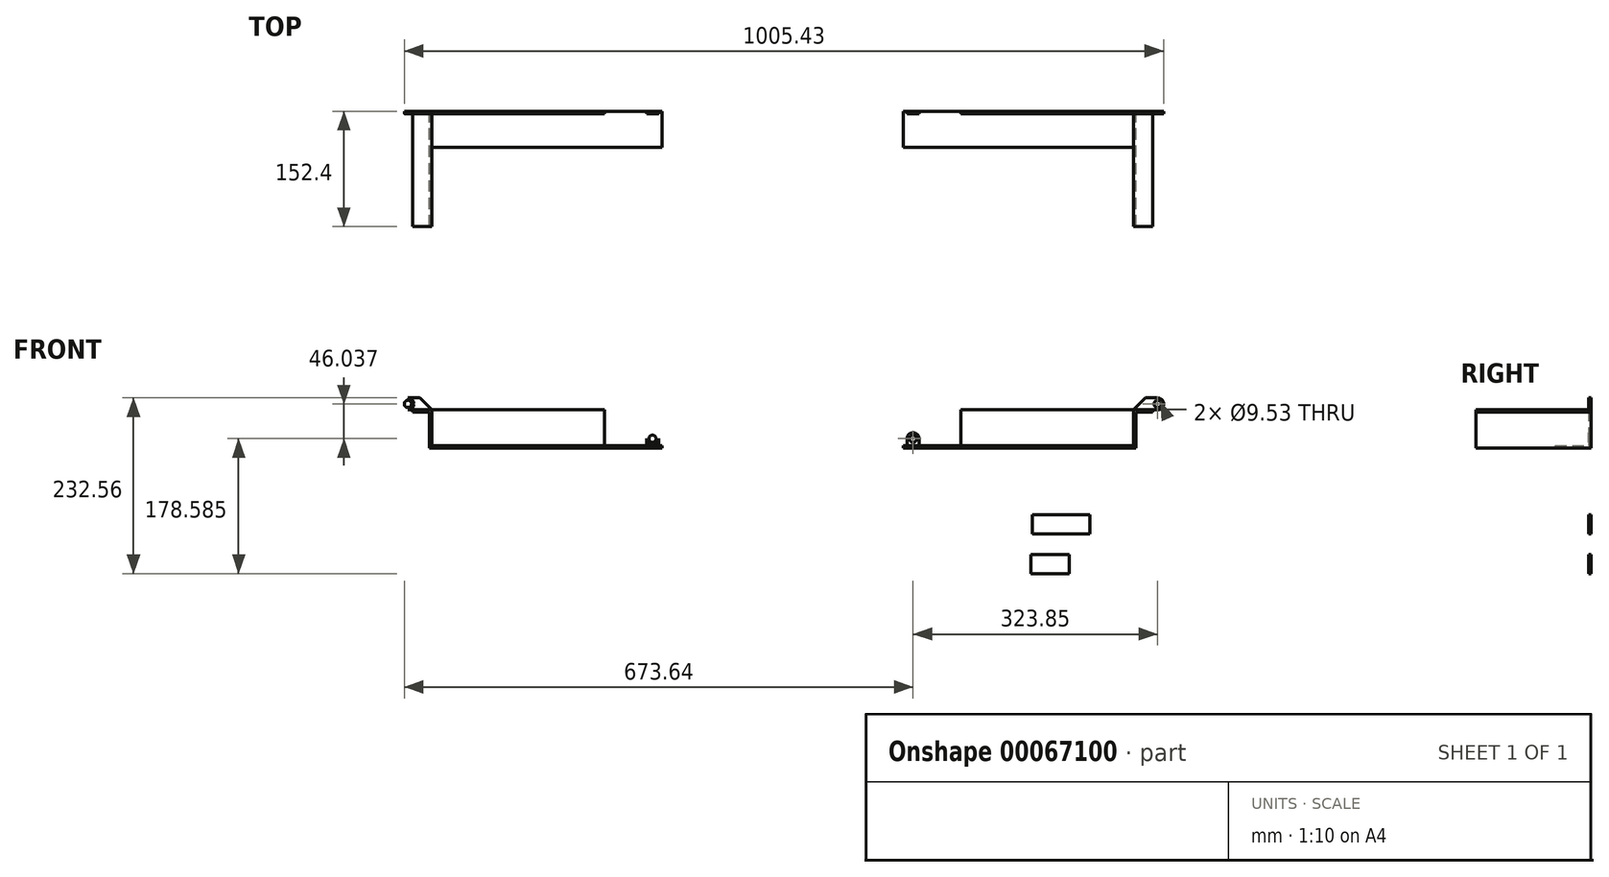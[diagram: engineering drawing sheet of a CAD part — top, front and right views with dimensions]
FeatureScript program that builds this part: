
annotation { "Feature Type Name" : "Feature", "Feature Type Description" : "" }
export const myFeature = defineFeature(function(context is Context, id is Id, definition is map)
    precondition{}
    {
        {
            var Q0;
            Q0=qCreatedBy(makeId("Front.planeOp"),FACE);
            var sketch = newSketch(context, id + "F0", { "sketchPlane" : qUnion([Q0])});
            skLineSegment(sketch, "E0", {"start": v(120.09, 92.83) * mm, "end": v(94.69, 92.83) * mm});
            skLineSegment(sketch, "E1", {"start": v(94.69, 92.83) * mm, "end": v(94.69, 42.03) * mm});
            skLineSegment(sketch, "E2", {"start": v(94.69, 42.03) * mm, "end": v(97.86, 42.03) * mm});
            skLineSegment(sketch, "E3", {"start": v(97.86, 42.03) * mm, "end": v(97.86, 89.66) * mm});
            skLineSegment(sketch, "E4", {"start": v(97.86, 89.66) * mm, "end": v(120.09, 89.66) * mm});
            skLineSegment(sketch, "E5", {"start": v(120.09, 89.66) * mm, "end": v(120.09, 92.83) * mm});
            skLineSegment(sketch, "E6", {"start": v(94.69, 92.83) * mm, "end": v(-133.91, 92.83) * mm});
            skLineSegment(sketch, "E7", {"start": v(-133.91, 92.83) * mm, "end": v(-133.91, 42.03) * mm});
            skLineSegment(sketch, "E8", {"start": v(-133.91, 42.03) * mm, "end": v(94.69, 42.03) * mm});
            skLineSegment(sketch, "E9", {"start": v(-133.91, 42.03) * mm, "end": v(-210.11, 42.03) * mm});
            skLineSegment(sketch, "E10", {"start": v(-210.11, 42.03) * mm, "end": v(-210.11, 45.2) * mm});
            skLineSegment(sketch, "E11", {"start": v(-210.11, 45.2) * mm, "end": v(-133.91, 45.2) * mm});
            skLineSegment(sketch, "E12", {"start": v(-184.71, 45.2) * mm, "end": v(-184.71, 42.03) * mm});
            skLineSegment(sketch, "E13", {"start": v(-184.71, 42.03) * mm, "end": v(-159.31, 42.03) * mm});
            skLineSegment(sketch, "E14", {"start": v(-159.31, 42.03) * mm, "end": v(-159.31, 45.2) * mm});
            skCircle(sketch, "E15", {"center": v(-197.41, 54.73) * mm, "radius": 7.94 * mm});
            skLineSegment(sketch, "E16", {"start": v(-205.35, 54.73) * mm, "end": v(-205.35, 45.2) * mm});
            skLineSegment(sketch, "E17", {"start": v(-189.47, 54.73) * mm, "end": v(-189.47, 45.2) * mm});
            skCircle(sketch, "E18", {"center": v(-197.41, 54.73) * mm, "radius": 4.76 * mm});
            skCircle(sketch, "E19", {"center": v(126.44, 100.77) * mm, "radius": 7.94 * mm});
            skCircle(sketch, "E20", {"center": v(126.44, 100.77) * mm, "radius": 4.76 * mm});
            skLineSegment(sketch, "E21", {"start": v(120.09, 92.83) * mm, "end": v(126.44, 92.83) * mm});
            skLineSegment(sketch, "E22", {"start": v(94.69, 92.83) * mm, "end": v(110.56, 108.7) * mm});
            skLineSegment(sketch, "E23", {"start": v(110.56, 108.7) * mm, "end": v(126.44, 108.7) * mm});
            skLineSegment(sketch, "E24", {"start": v(-184.71, 42.03) * mm, "end": v(-159.31, 45.2) * mm, "construction": true});
            skLineSegment(sketch, "E25", {"start": v(-197.41, 40.48) * mm, "end": v(-197.41, 98.92) * mm, "construction": true});
            skLineSegment(sketch, "E26", {"start": v(-210.11, 42.03) * mm, "end": v(-184.71, 45.2) * mm, "construction": true});
            skLineSegment(sketch, "E27", {"start": v(-197.41, 43.62) * mm, "end": v(-197.41, 100.75) * mm, "construction": true});
            skLineSegment(sketch, "E28", {"start": v(-369.92, 208.5) * mm, "end": v(-369.92, -62.68) * mm, "construction": true});
            skLineSegment(sketch, "E29.MirrorCS", {"start": v(-529.74, 42.03) * mm, "end": v(-555.14, 45.2) * mm, "construction": true});
            skLineSegment(sketch, "E30.MirrorCS", {"start": v(-550.38, 54.73) * mm, "end": v(-550.38, 45.2) * mm});
            skLineSegment(sketch, "E31.MirrorCS", {"start": v(-834.54, 42.03) * mm, "end": v(-837.71, 42.03) * mm});
            skLineSegment(sketch, "E32.MirrorCS", {"start": v(-529.74, 42.03) * mm, "end": v(-529.74, 45.2) * mm});
            skLineSegment(sketch, "E33.MirrorCS", {"start": v(-534.5, 54.73) * mm, "end": v(-534.5, 45.2) * mm});
            skLineSegment(sketch, "E34.MirrorCS", {"start": v(-859.94, 92.83) * mm, "end": v(-866.29, 92.83) * mm});
            skCircle(sketch, "E35.MirrorC", {"center": v(-866.29, 100.77) * mm, "radius": 4.76 * mm});
            skLineSegment(sketch, "E36.MirrorCS", {"start": v(-555.14, 45.2) * mm, "end": v(-555.14, 42.03) * mm});
            skLineSegment(sketch, "E37.MirrorCS", {"start": v(-859.94, 89.66) * mm, "end": v(-859.94, 92.83) * mm});
            skLineSegment(sketch, "E38.MirrorCS", {"start": v(-555.14, 42.03) * mm, "end": v(-580.54, 45.2) * mm, "construction": true});
            skCircle(sketch, "E39.MirrorC", {"center": v(-542.44, 54.73) * mm, "radius": 4.76 * mm});
            skLineSegment(sketch, "E40.MirrorCS", {"start": v(-580.54, 42.03) * mm, "end": v(-580.54, 45.2) * mm});
            skLineSegment(sketch, "E41.MirrorCS", {"start": v(-555.14, 42.03) * mm, "end": v(-580.54, 42.03) * mm});
            skLineSegment(sketch, "E42.MirrorCS", {"start": v(-542.44, 43.62) * mm, "end": v(-542.44, 100.75) * mm, "construction": true});
            skCircle(sketch, "E43.MirrorC", {"center": v(-866.29, 100.77) * mm, "radius": 7.94 * mm});
            skLineSegment(sketch, "E44.MirrorCS", {"start": v(-850.41, 108.7) * mm, "end": v(-866.29, 108.7) * mm});
            skLineSegment(sketch, "E45.MirrorCS", {"start": v(-542.44, 40.48) * mm, "end": v(-542.44, 98.92) * mm, "construction": true});
            skCircle(sketch, "E46.MirrorC", {"center": v(-542.44, 54.73) * mm, "radius": 7.94 * mm});
            skLineSegment(sketch, "E47.MirrorCS", {"start": v(-529.74, 45.2) * mm, "end": v(-605.94, 45.2) * mm});
            skLineSegment(sketch, "E48.MirrorCS", {"start": v(-605.94, 42.03) * mm, "end": v(-529.74, 42.03) * mm});
            skLineSegment(sketch, "E49.MirrorCS", {"start": v(-834.54, 92.83) * mm, "end": v(-850.41, 108.7) * mm});
            skLineSegment(sketch, "E50.MirrorCS", {"start": v(-859.94, 92.83) * mm, "end": v(-834.54, 92.83) * mm});
            skLineSegment(sketch, "E51.MirrorCS", {"start": v(-837.71, 42.03) * mm, "end": v(-837.71, 89.66) * mm});
            skLineSegment(sketch, "E52.MirrorCS", {"start": v(-837.71, 89.66) * mm, "end": v(-859.94, 89.66) * mm});
            skLineSegment(sketch, "E53.MirrorCS", {"start": v(-834.54, 92.83) * mm, "end": v(-605.94, 92.83) * mm});
            skLineSegment(sketch, "E54.MirrorCS", {"start": v(-605.94, 92.83) * mm, "end": v(-605.94, 42.03) * mm});
            skLineSegment(sketch, "E55.MirrorCS", {"start": v(-834.54, 92.83) * mm, "end": v(-834.54, 42.03) * mm});
            skLineSegment(sketch, "E56.MirrorCS", {"start": v(-605.94, 42.03) * mm, "end": v(-834.54, 42.03) * mm});
            skLineSegment(sketch, "E57", {"start": v(-605.94, 45.2) * mm, "end": v(-834.54, 45.2) * mm});
            skLineSegment(sketch, "E58", {"start": v(-133.91, 45.2) * mm, "end": v(94.69, 45.2) * mm});
            skSolve(sketch);
        }
        {
            var Q0;
            Q0=makeQuery(id+"F0.imprint","IMPRINT",FACE,{"disambiguationData":[TD([[makeQuery(id+"F0.imprint","IMPRINT",EDGE,{"derivedFrom":sQuery(id+"F0.wireOp",EDGE,"E31.MirrorCS")}),-1.0]])]});
            var Q1;
            {var subQ0=sQuery(id+"F0.wireOp",EDGE,"E1");Q1=makeQuery(id+"F0.imprint","IMPRINT",FACE,{"disambiguationData":[TD([[makeQuery(id+"F0.imprint","IMPRINT",EDGE,{"derivedFrom":subQ0}),1.0]])]});}
            extrude(context, id + "F1", {"entities" : qUnion([Q0, Q1]), "depth" : 152.4 * mm});
        }
        {
            var Q0;
            Q0=makeQuery(id+"F0.imprint","IMPRINT",FACE,{"disambiguationData":[TD([[makeQuery(id+"F0.imprint","IMPRINT",EDGE,{"derivedFrom":sQuery(id+"F0.wireOp",EDGE,"E35.MirrorC")}),1.0]])]});
            var Q1;
            {var subQ3=sQuery(id+"F0.wireOp",EDGE,"E34.MirrorCS");Q1=makeQuery(id+"F0.imprint","IMPRINT",FACE,{"disambiguationData":[TD([[makeQuery(id+"F0.imprint","IMPRINT",EDGE,{"derivedFrom":subQ3}),-1.0]])]});}
            var Q2;
            {var subQ1=sQuery(id+"F0.wireOp",EDGE,"E21");Q2=makeQuery(id+"F0.imprint","IMPRINT",FACE,{"disambiguationData":[TD([[makeQuery(id+"F0.imprint","IMPRINT",EDGE,{"derivedFrom":subQ1}),1.0]])]});}
            var Q3;
            Q3=makeQuery(id+"F0.imprint","IMPRINT",FACE,{"disambiguationData":[TD([[makeQuery(id+"F0.imprint","IMPRINT",EDGE,{"derivedFrom":sQuery(id+"F0.wireOp",EDGE,"E20")}),-1.0]])]});
            var Q4;
            {var subQ0=sQuery(id+"F0.wireOp",EDGE,"E30.MirrorCS");Q4=makeQuery(id+"F0.imprint","IMPRINT",FACE,{"disambiguationData":[TD([[makeQuery(id+"F0.imprint","IMPRINT",EDGE,{"derivedFrom":subQ0}),1.0]])]});}
            var Q5;
            Q5=makeQuery(id+"F0.imprint","IMPRINT",FACE,{"disambiguationData":[TD([[makeQuery(id+"F0.imprint","IMPRINT",EDGE,{"derivedFrom":sQuery(id+"F0.wireOp",EDGE,"E39.MirrorC")}),1.0]])]});
            var Q6;
            Q6=makeQuery(id+"F0.imprint","IMPRINT",FACE,{"disambiguationData":[TD([[makeQuery(id+"F0.imprint","IMPRINT",EDGE,{"derivedFrom":sQuery(id+"F0.wireOp",EDGE,"E18")}),-1.0]])]});
            var Q7;
            {var subQ0=sQuery(id+"F0.wireOp",EDGE,"E16");Q7=makeQuery(id+"F0.imprint","IMPRINT",FACE,{"disambiguationData":[TD([[makeQuery(id+"F0.imprint","IMPRINT",EDGE,{"derivedFrom":subQ0}),1.0]])]});}
            extrude(context, id + "F2", {"entities" : qUnion([Q0, Q1, Q2, Q3, Q4, Q5, Q6, Q7]), "depth" : 3.17 * mm});
        }
        {
            var Q0;
            {var subQ2=sQuery(id+"F0.wireOp",EDGE,"E56.MirrorCS");Q0=makeQuery(id+"F0.imprint","IMPRINT",FACE,{"disambiguationData":[TD([[makeQuery(id+"F0.imprint","IMPRINT",EDGE,{"derivedFrom":subQ2}),-1.0]])]});}
            var Q1;
            {var subQ0=sQuery(id+"F0.wireOp",EDGE,"E40.MirrorCS");Q1=makeQuery(id+"F0.imprint","IMPRINT",FACE,{"disambiguationData":[TD([[makeQuery(id+"F0.imprint","IMPRINT",EDGE,{"derivedFrom":subQ0}),1.0]])]});}
            var Q2;
            {var subQ0=sQuery(id+"F0.wireOp",EDGE,"E36.MirrorCS");Q2=makeQuery(id+"F0.imprint","IMPRINT",FACE,{"disambiguationData":[TD([[makeQuery(id+"F0.imprint","IMPRINT",EDGE,{"derivedFrom":subQ0}),-1.0]])]});}
            var Q3;
            {var subQ4=sQuery(id+"F0.wireOp",EDGE,"E32.MirrorCS");Q3=makeQuery(id+"F0.imprint","IMPRINT",FACE,{"disambiguationData":[TD([[makeQuery(id+"F0.imprint","IMPRINT",EDGE,{"derivedFrom":subQ4}),1.0]])]});}
            var Q4;
            {var subQ3=sQuery(id+"F0.wireOp",EDGE,"E10");Q4=makeQuery(id+"F0.imprint","IMPRINT",FACE,{"disambiguationData":[TD([[makeQuery(id+"F0.imprint","IMPRINT",EDGE,{"derivedFrom":subQ3}),-1.0]])]});}
            var Q5;
            {var subQ0=sQuery(id+"F0.wireOp",EDGE,"E12");Q5=makeQuery(id+"F0.imprint","IMPRINT",FACE,{"disambiguationData":[TD([[makeQuery(id+"F0.imprint","IMPRINT",EDGE,{"derivedFrom":subQ0}),1.0]])]});}
            var Q6;
            {var subQ5=sQuery(id+"F0.wireOp",EDGE,"E14");Q6=makeQuery(id+"F0.imprint","IMPRINT",FACE,{"disambiguationData":[TD([[makeQuery(id+"F0.imprint","IMPRINT",EDGE,{"derivedFrom":subQ5}),-1.0]])]});}
            var Q7;
            {var subQ0=sQuery(id+"F0.wireOp",EDGE,"E8");Q7=makeQuery(id+"F0.imprint","IMPRINT",FACE,{"disambiguationData":[TD([[makeQuery(id+"F0.imprint","IMPRINT",EDGE,{"derivedFrom":subQ0}),1.0]])]});}
            extrude(context, id + "F3", {"entities" : qUnion([Q0, Q1, Q2, Q3, Q4, Q5, Q6, Q7]), "depth" : 47.62 * mm});
        }
        {
            var Q0;
            {var subQ0=sQuery(id+"F0.wireOp",EDGE,"E53.MirrorCS");Q0=makeQuery(id+"F0.imprint","IMPRINT",FACE,{"disambiguationData":[TD([[makeQuery(id+"F0.imprint","IMPRINT",EDGE,{"derivedFrom":subQ0}),-1.0]])]});}
            var Q1;
            {var subQ0=sQuery(id+"F0.wireOp",EDGE,"E6");Q1=makeQuery(id+"F0.imprint","IMPRINT",FACE,{"disambiguationData":[TD([[makeQuery(id+"F0.imprint","IMPRINT",EDGE,{"derivedFrom":subQ0}),1.0]])]});}
            extrude(context, id + "F4", {"entities" : qUnion([Q0, Q1]), "depth" : 3.17 * mm});
        }
        {
            var Q0;
            Q0=qCreatedBy(makeId("Front.planeOp"),FACE);
            var sketch = newSketch(context, id + "F5", { "sketchPlane" : qUnion([Q0])});
            skLineSegment(sketch, "E59.bottom", {"start": v(-39.87, -46.07) * mm, "end": v(36.33, -46.07) * mm});
            skLineSegment(sketch, "E59.top", {"start": v(-39.87, -71.47) * mm, "end": v(36.33, -71.47) * mm});
            skLineSegment(sketch, "E59.left", {"start": v(-39.87, -46.07) * mm, "end": v(-39.87, -71.47) * mm});
            skLineSegment(sketch, "E59.right", {"start": v(36.33, -46.07) * mm, "end": v(36.33, -71.47) * mm});
            skLineSegment(sketch, "E60.bottom", {"start": v(-41.78, -98.45) * mm, "end": v(9.02, -98.45) * mm});
            skLineSegment(sketch, "E60.top", {"start": v(-41.78, -123.85) * mm, "end": v(9.02, -123.85) * mm});
            skLineSegment(sketch, "E60.left", {"start": v(-41.78, -98.45) * mm, "end": v(-41.78, -123.85) * mm});
            skLineSegment(sketch, "E60.right", {"start": v(9.02, -98.45) * mm, "end": v(9.02, -123.85) * mm});
            skSolve(sketch);
        }
        {
            var Q0;
            Q0=makeQuery(id+"F5.imprint","IMPRINT",FACE,{"disambiguationData":[TD([[makeQuery(id+"F5.imprint","IMPRINT",EDGE,{"derivedFrom":sQuery(id+"F5.wireOp",EDGE,"E59.bottom")}),-1.0]])]});
            var Q1;
            Q1=makeQuery(id+"F5.imprint","IMPRINT",FACE,{"disambiguationData":[TD([[makeQuery(id+"F5.imprint","IMPRINT",EDGE,{"derivedFrom":sQuery(id+"F5.wireOp",EDGE,"E60.bottom")}),-1.0]])]});
            extrude(context, id + "F6", {"entities" : qUnion([Q0, Q1]), "depth" : 3.17 * mm});
        }
    });
